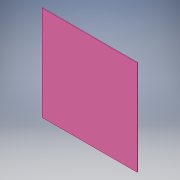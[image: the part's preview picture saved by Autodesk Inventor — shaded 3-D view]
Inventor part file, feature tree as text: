
AUTODESK INVENTOR PART (.ipt)
format: ipt  version: 2018 (Build 220112000, 112)  size: 89,088 bytes
history: native  units: mm
features: extrude x1, sketch x1
ambient origin geometry x8: Origin, YZ Plane, XZ Plane, XY Plane, X Axis, Y Axis, Z Axis, Center Point
bodies: Solid1 (feature_tree)
feature tree (2):
  extrude  "Extrusion1"  Depth=250.0mm
  sketch  "Sketch1"  dims[d0=250.0mm d1=250.0mm d2=1.6mm d3=0.0mm]
